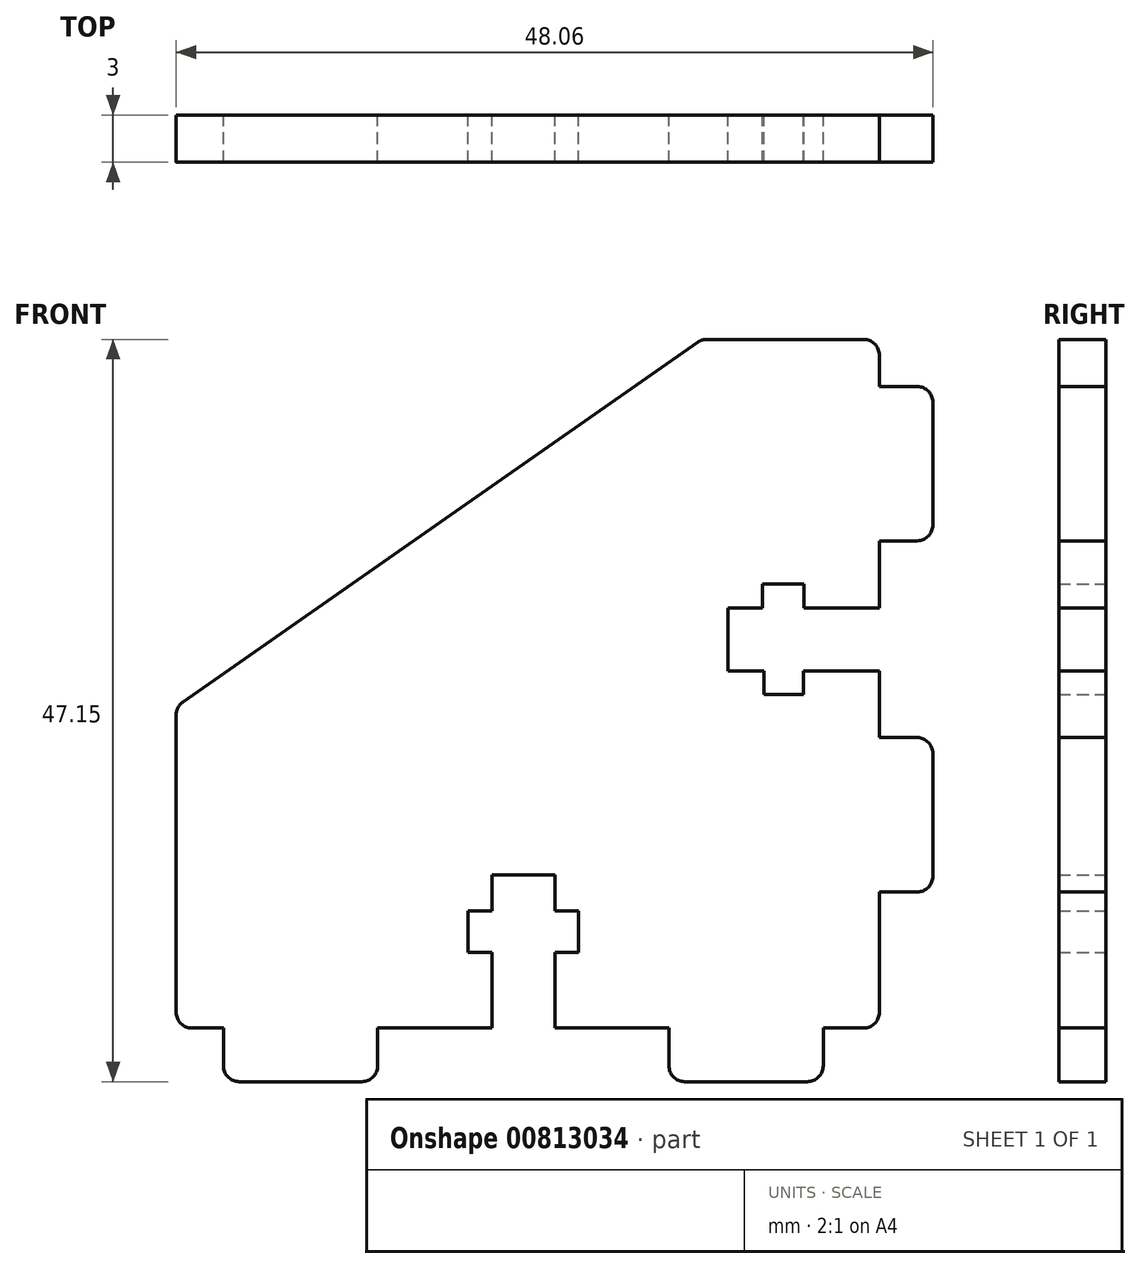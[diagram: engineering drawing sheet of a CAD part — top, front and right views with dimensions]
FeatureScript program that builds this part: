
annotation { "Feature Type Name" : "Feature", "Feature Type Description" : "" }
export const myFeature = defineFeature(function(context is Context, id is Id, definition is map)
    precondition{}
    {
        {
            var Q0;
            Q0=qCreatedBy(makeId("Front.planeOp"),FACE);
            var sketch = newSketch(context, id + "F0", { "sketchPlane" : qUnion([Q0])});
            skLineSegment(sketch, "E0.bottom", {"start": v(19, 63.11) * mm, "end": v(16.6, 63.11) * mm});
            skLineSegment(sketch, "E0.top", {"start": v(19, 53.31) * mm, "end": v(16.6, 53.31) * mm});
            skLineSegment(sketch, "E0.left", {"start": v(20, 62.11) * mm, "end": v(20, 54.31) * mm});
            skLineSegment(sketch, "E1.bottom", {"start": v(16.6, 40.81) * mm, "end": v(19, 40.81) * mm});
            skLineSegment(sketch, "E1.top", {"start": v(16.6, 31.01) * mm, "end": v(19, 31.01) * mm});
            skLineSegment(sketch, "E1.right", {"start": v(20, 39.81) * mm, "end": v(20, 32.01) * mm});
            skLineSegment(sketch, "E2", {"start": v(13.03, 22.36) * mm, "end": v(13.03, 19.96) * mm});
            skLineSegment(sketch, "E3", {"start": v(12.03, 18.96) * mm, "end": v(4.23, 18.96) * mm});
            skLineSegment(sketch, "E4", {"start": v(3.23, 19.96) * mm, "end": v(3.23, 22.36) * mm});
            skLineSegment(sketch, "E5", {"start": v(-15.27, 22.36) * mm, "end": v(-15.27, 19.96) * mm});
            skLineSegment(sketch, "E6", {"start": v(-16.27, 18.96) * mm, "end": v(-24.07, 18.96) * mm});
            skLineSegment(sketch, "E7", {"start": v(-25.07, 19.96) * mm, "end": v(-25.07, 22.36) * mm});
            skLineSegment(sketch, "E8", {"start": v(-25.07, 22.36) * mm, "end": v(-27.07, 22.36) * mm});
            skLineSegment(sketch, "E9", {"start": v(-28.07, 23.36) * mm, "end": v(-28.07, 42.26) * mm});
            skLineSegment(sketch, "E10", {"start": v(-27.64, 43.08) * mm, "end": v(5.06, 65.93) * mm});
            skLineSegment(sketch, "E11", {"start": v(5.64, 66.11) * mm, "end": v(15.6, 66.11) * mm});
            skLineSegment(sketch, "E12", {"start": v(16.6, 65.11) * mm, "end": v(16.6, 63.11) * mm});
            skLineSegment(sketch, "E13", {"start": v(13.03, 22.36) * mm, "end": v(15.6, 22.36) * mm});
            skLineSegment(sketch, "E14", {"start": v(16.6, 31.01) * mm, "end": v(16.6, 23.36) * mm});
            skPoint(sketch, "E15.visualSharp", {"position": v(16.6, 22.36) * mm});
            skArc(sketch, "E15.filletArc", {"start": v(15.6, 22.36) * mm, "mid": v(16.3, 22.65) * mm, "end": v(16.6, 23.36) * mm});
            skPoint(sketch, "E16.visualSharp", {"position": v(20, 31.01) * mm});
            skArc(sketch, "E16.filletArc", {"start": v(19, 31.01) * mm, "mid": v(19.7, 31.3) * mm, "end": v(20, 32.01) * mm});
            skPoint(sketch, "E17.visualSharp", {"position": v(20, 40.81) * mm});
            skArc(sketch, "E17.filletArc", {"start": v(20, 39.81) * mm, "mid": v(19.7, 40.52) * mm, "end": v(19, 40.81) * mm});
            skPoint(sketch, "E18.visualSharp", {"position": v(20, 53.31) * mm});
            skArc(sketch, "E18.filletArc", {"start": v(19, 53.31) * mm, "mid": v(19.7, 53.6) * mm, "end": v(20, 54.31) * mm});
            skPoint(sketch, "E19.visualSharp", {"position": v(20, 63.11) * mm});
            skArc(sketch, "E19.filletArc", {"start": v(20, 62.11) * mm, "mid": v(19.7, 62.82) * mm, "end": v(19, 63.11) * mm});
            skPoint(sketch, "E20.visualSharp", {"position": v(16.6, 66.11) * mm});
            skArc(sketch, "E20.filletArc", {"start": v(16.6, 65.11) * mm, "mid": v(16.3, 65.82) * mm, "end": v(15.6, 66.11) * mm});
            skPoint(sketch, "E21.visualSharp", {"position": v(5.32, 66.11) * mm});
            skArc(sketch, "E21.filletArc", {"start": v(5.64, 66.11) * mm, "mid": v(5.34, 66.07) * mm, "end": v(5.06, 65.93) * mm});
            skPoint(sketch, "E22.visualSharp", {"position": v(-28.07, 42.78) * mm});
            skArc(sketch, "E22.filletArc", {"start": v(-27.64, 43.08) * mm, "mid": v(-27.96, 42.72) * mm, "end": v(-28.07, 42.26) * mm});
            skPoint(sketch, "E23.visualSharp", {"position": v(-28.07, 22.36) * mm});
            skArc(sketch, "E23.filletArc", {"start": v(-28.07, 23.36) * mm, "mid": v(-27.78, 22.65) * mm, "end": v(-27.07, 22.36) * mm});
            skPoint(sketch, "E24.visualSharp", {"position": v(-25.07, 18.96) * mm});
            skArc(sketch, "E24.filletArc", {"start": v(-25.07, 19.96) * mm, "mid": v(-24.78, 19.25) * mm, "end": v(-24.07, 18.96) * mm});
            skPoint(sketch, "E25.visualSharp", {"position": v(-15.27, 18.96) * mm});
            skArc(sketch, "E25.filletArc", {"start": v(-16.27, 18.96) * mm, "mid": v(-15.56, 19.25) * mm, "end": v(-15.27, 19.96) * mm});
            skPoint(sketch, "E26.visualSharp", {"position": v(3.23, 18.96) * mm});
            skArc(sketch, "E26.filletArc", {"start": v(3.23, 19.96) * mm, "mid": v(3.52, 19.25) * mm, "end": v(4.23, 18.96) * mm});
            skPoint(sketch, "E27.visualSharp", {"position": v(13.03, 18.96) * mm});
            skArc(sketch, "E27.filletArc", {"start": v(12.03, 18.96) * mm, "mid": v(12.74, 19.25) * mm, "end": v(13.03, 19.96) * mm});
            skLineSegment(sketch, "E28.left", {"start": v(6.97, 49.06) * mm, "end": v(6.98, 45.06) * mm});
            skLineSegment(sketch, "E29.top", {"start": v(9.26, 43.56) * mm, "end": v(11.76, 43.56) * mm});
            skPoint(sketch, "E30", {"position": v(9.17, 49.06) * mm});
            skPoint(sketch, "E31", {"position": v(11.8, 49.06) * mm});
            skPoint(sketch, "E32", {"position": v(9.28, 45.06) * mm});
            skPoint(sketch, "E33", {"position": v(11.78, 45.06) * mm});
            skLineSegment(sketch, "E34", {"start": v(16.6, 49.06) * mm, "end": v(11.8, 49.06) * mm});
            skLineSegment(sketch, "E35", {"start": v(11.8, 50.56) * mm, "end": v(11.8, 49.06) * mm});
            skLineSegment(sketch, "E36", {"start": v(9.17, 50.56) * mm, "end": v(9.17, 49.06) * mm});
            skLineSegment(sketch, "E37", {"start": v(6.97, 49.06) * mm, "end": v(9.17, 49.06) * mm});
            skLineSegment(sketch, "E38", {"start": v(6.98, 45.06) * mm, "end": v(9.28, 45.06) * mm});
            skLineSegment(sketch, "E39", {"start": v(9.28, 45.06) * mm, "end": v(9.26, 43.56) * mm});
            skLineSegment(sketch, "E40", {"start": v(11.78, 45.06) * mm, "end": v(11.76, 43.56) * mm});
            skLineSegment(sketch, "E41", {"start": v(11.78, 45.06) * mm, "end": v(16.6, 45.06) * mm});
            skLineSegment(sketch, "E42", {"start": v(16.6, 53.31) * mm, "end": v(16.6, 49.06) * mm});
            skLineSegment(sketch, "E43", {"start": v(16.6, 45.06) * mm, "end": v(16.6, 40.81) * mm});
            skLineSegment(sketch, "E44", {"start": v(9.17, 50.56) * mm, "end": v(11.8, 50.56) * mm});
            skLineSegment(sketch, "E45", {"start": v(-8.02, 22.36) * mm, "end": v(-8.02, 27.18) * mm});
            skLineSegment(sketch, "E46", {"start": v(-8.02, 27.18) * mm, "end": v(-9.52, 27.18) * mm});
            skLineSegment(sketch, "E47", {"start": v(-9.52, 27.18) * mm, "end": v(-9.52, 29.8) * mm});
            skLineSegment(sketch, "E48", {"start": v(-9.52, 29.8) * mm, "end": v(-8.02, 29.8) * mm});
            skLineSegment(sketch, "E49", {"start": v(-8.02, 29.8) * mm, "end": v(-8.02, 32.1) * mm});
            skLineSegment(sketch, "E50", {"start": v(-8.02, 32.1) * mm, "end": v(-4.02, 32.1) * mm});
            skLineSegment(sketch, "E51", {"start": v(-4.02, 32.1) * mm, "end": v(-4.02, 29.8) * mm});
            skLineSegment(sketch, "E52", {"start": v(-4.02, 29.8) * mm, "end": v(-2.52, 29.8) * mm});
            skLineSegment(sketch, "E53", {"start": v(-2.52, 29.8) * mm, "end": v(-2.52, 27.18) * mm});
            skLineSegment(sketch, "E54", {"start": v(-2.52, 27.18) * mm, "end": v(-4.02, 27.18) * mm});
            skLineSegment(sketch, "E55", {"start": v(-4.02, 27.18) * mm, "end": v(-4.02, 22.36) * mm});
            skLineSegment(sketch, "E56", {"start": v(-15.27, 22.36) * mm, "end": v(-8.02, 22.36) * mm});
            skLineSegment(sketch, "E57", {"start": v(-4.02, 22.36) * mm, "end": v(3.23, 22.36) * mm});
            skSolve(sketch);
        }
        {
            var Q0;
            Q0 = qSketchRegion(id + "F0", true);
            extrude(context, id + "F1", {"entities" : qUnion([Q0]), "depth" : 3 * mm, "offsetDistance" : 25 * mm});
        }
        {
            var Q0;
            Q0 = qSketchRegion(id + "F0", true);
            extrude(context, id + "F2", {"entities" : qUnion([Q0]), "operationType" : NewBodyOperationType.ADD, "depth" : 3 * mm, "offsetDistance" : 25 * mm});
        }
    });
